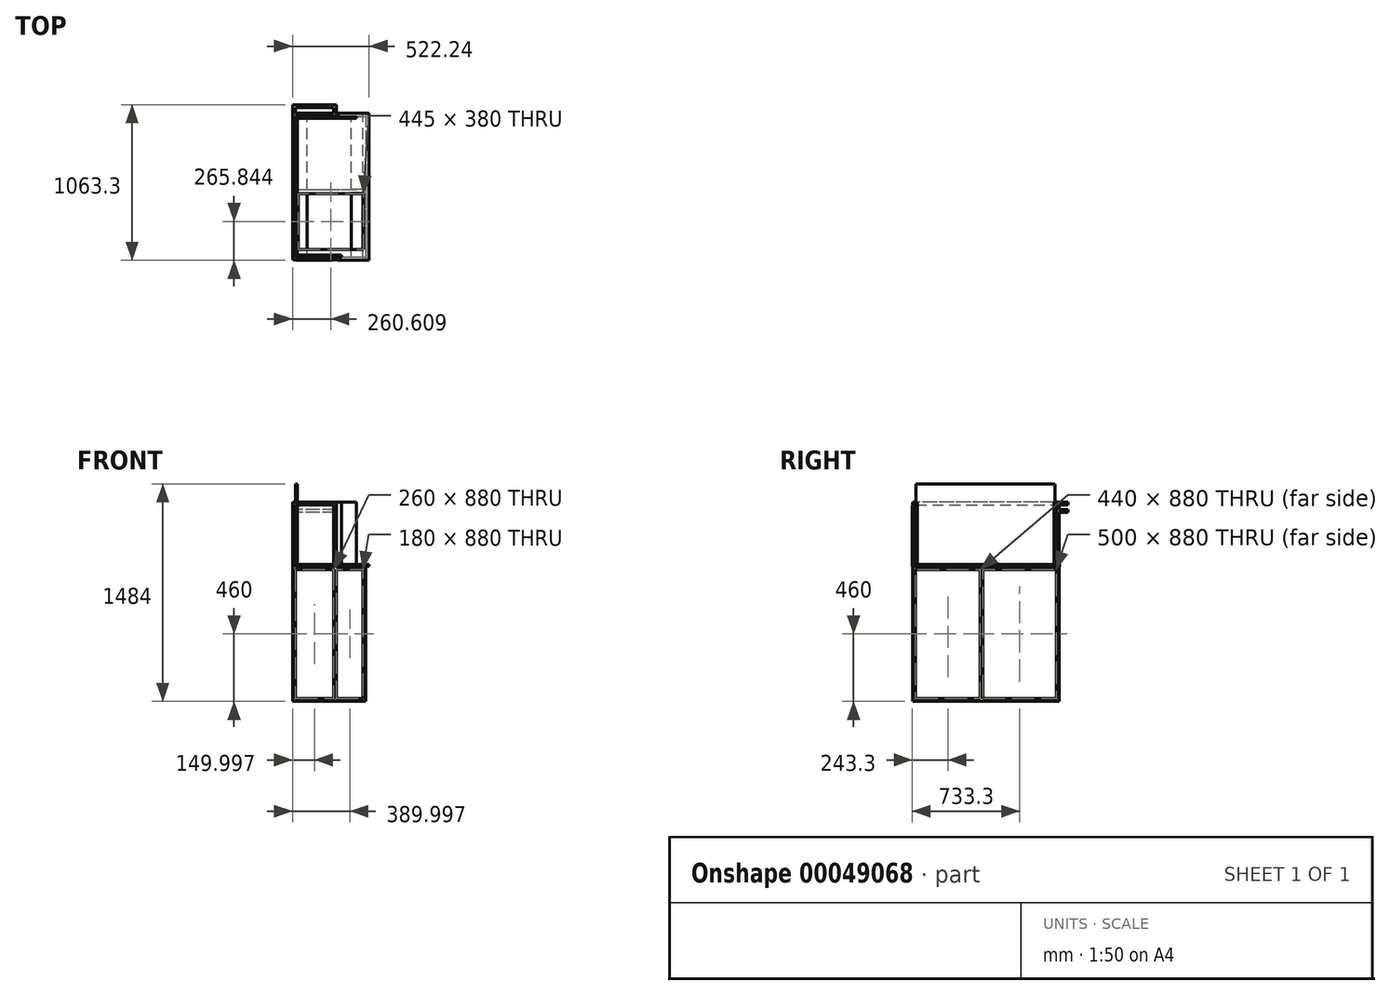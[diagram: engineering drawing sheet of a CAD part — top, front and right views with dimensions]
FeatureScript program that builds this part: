
annotation { "Feature Type Name" : "Feature", "Feature Type Description" : "" }
export const myFeature = defineFeature(function(context is Context, id is Id, definition is map)
    precondition{}
    {
        {
            var Q0;
            Q0=qCreatedBy(makeId("Top.planeOp"),FACE);
            var sketch = newSketch(context, id + "F0", { "sketchPlane" : qUnion([Q0])});
            skLineSegment(sketch, "E0.bottom", {"start": v(-100.51, 520.1) * mm, "end": v(399.49, 520.1) * mm});
            skLineSegment(sketch, "E0.top", {"start": v(-100.51, -479.9) * mm, "end": v(399.49, -479.9) * mm});
            skLineSegment(sketch, "E0.left", {"start": v(-100.51, 520.1) * mm, "end": v(-100.51, -479.9) * mm});
            skLineSegment(sketch, "E0.right", {"start": v(399.49, 520.1) * mm, "end": v(399.49, -479.9) * mm});
            skLineSegment(sketch, "E1.bottom", {"start": v(-80.51, 500.1) * mm, "end": v(379.49, 500.1) * mm});
            skLineSegment(sketch, "E1.top", {"start": v(-80.51, -459.9) * mm, "end": v(379.49, -459.9) * mm});
            skLineSegment(sketch, "E1.left", {"start": v(-80.51, 500.1) * mm, "end": v(-80.51, -459.9) * mm});
            skLineSegment(sketch, "E1.right", {"start": v(379.49, 500.1) * mm, "end": v(379.49, -459.9) * mm});
            skSolve(sketch);
        }
        {
            var Q0;
            Q0=makeQuery(id+"F0.imprint","IMPRINT",FACE,{"disambiguationData":[TD([[makeQuery(id+"F0.imprint","IMPRINT",EDGE,{"derivedFrom":sQuery(id+"F0.wireOp",EDGE,"E0.bottom")}),-1.0]])]});
            extrude(context, id + "F1", {"entities" : qUnion([Q0]), "depth" : 20 * mm});
        }
        {
            var Q0;
            Q0=makeQuery(id+"F1.opExtrude","CAP_FACE",FACE,{"disambiguationData":[OSD([sQuery(id+"F0.wireOp",EDGE,"E0.bottom"),sQuery(id+"F0.wireOp",EDGE,"E0.top"),sQuery(id+"F0.wireOp",EDGE,"E0.left"),sQuery(id+"F0.wireOp",EDGE,"E0.right"),sQuery(id+"F0.wireOp",EDGE,"E1.bottom"),sQuery(id+"F0.wireOp",EDGE,"E1.top"),sQuery(id+"F0.wireOp",EDGE,"E1.left"),sQuery(id+"F0.wireOp",EDGE,"E1.right")])],"isStart":false});
            var sketch = newSketch(context, id + "F2", { "sketchPlane" : qUnion([Q0])});
            skLineSegment(sketch, "E2.bottom", {"start": v(-100.51, 520.1) * mm, "end": v(-80.51, 520.1) * mm});
            skLineSegment(sketch, "E2.top", {"start": v(-100.51, 500.1) * mm, "end": v(-80.51, 500.1) * mm});
            skLineSegment(sketch, "E2.left", {"start": v(-100.51, 520.1) * mm, "end": v(-100.51, 500.1) * mm});
            skLineSegment(sketch, "E2.right", {"start": v(-80.51, 520.1) * mm, "end": v(-80.51, 500.1) * mm});
            skLineSegment(sketch, "E3.bottom", {"start": v(-100.51, -479.9) * mm, "end": v(-80.51, -479.9) * mm});
            skLineSegment(sketch, "E3.top", {"start": v(-100.51, -459.9) * mm, "end": v(-80.51, -459.9) * mm});
            skLineSegment(sketch, "E3.left", {"start": v(-100.51, -479.9) * mm, "end": v(-100.51, -459.9) * mm});
            skLineSegment(sketch, "E3.right", {"start": v(-80.51, -479.9) * mm, "end": v(-80.51, -459.9) * mm});
            skLineSegment(sketch, "E4.bottom", {"start": v(179.49, -459.9) * mm, "end": v(199.49, -459.9) * mm});
            skLineSegment(sketch, "E4.top", {"start": v(179.49, -479.9) * mm, "end": v(199.49, -479.9) * mm});
            skLineSegment(sketch, "E4.left", {"start": v(199.49, -459.9) * mm, "end": v(199.49, -479.9) * mm});
            skLineSegment(sketch, "E4.right", {"start": v(179.49, -459.9) * mm, "end": v(179.49, -479.9) * mm});
            skLineSegment(sketch, "E5.bottom", {"start": v(179.49, 520.1) * mm, "end": v(199.49, 520.1) * mm});
            skLineSegment(sketch, "E5.top", {"start": v(179.49, 500.1) * mm, "end": v(199.49, 500.1) * mm});
            skLineSegment(sketch, "E5.left", {"start": v(179.49, 520.1) * mm, "end": v(179.49, 500.1) * mm});
            skLineSegment(sketch, "E5.right", {"start": v(199.49, 520.1) * mm, "end": v(199.49, 500.1) * mm});
            skSolve(sketch);
        }
        {
            var Q0;
            Q0 = qSketchRegion(id + "F2", true);
            extrude(context, id + "F3", {"entities" : qUnion([Q0]), "operationType" : NewBodyOperationType.ADD, "depth" : 1340 * mm});
        }
        {
            var Q0;
            {var subQ0=sQuery(id+"F0.wireOp",EDGE,"E0.bottom");var subQ1=sQuery(id+"F0.wireOp",EDGE,"E0.top");var subQ2=sQuery(id+"F0.wireOp",EDGE,"E0.right");var subQ3=sQuery(id+"F0.wireOp",EDGE,"E1.bottom");var subQ4=sQuery(id+"F0.wireOp",EDGE,"E1.top");var subQ5=sQuery(id+"F0.wireOp",EDGE,"E1.right");Q0=makeQuery(id+"F3.boolean.opBoolean","SPLIT",FACE,{"disambiguationData":[TD([makeQuery(id+"F1.opExtrude","SWEPT_FACE",FACE,{"disambiguationData":[OSD([subQ2])]})])],"derivedFrom":makeQuery(id+"F1.opExtrude","CAP_FACE",FACE,{"disambiguationData":[OSD([subQ0,subQ1,sQuery(id+"F0.wireOp",EDGE,"E0.left"),subQ2,subQ3,subQ4,sQuery(id+"F0.wireOp",EDGE,"E1.left"),subQ5])],"isStart":false})});}
            var sketch = newSketch(context, id + "F4", { "sketchPlane" : qUnion([Q0])});
            skLineSegment(sketch, "E6.bottom", {"start": v(379.49, 500.1) * mm, "end": v(399.49, 500.1) * mm});
            skLineSegment(sketch, "E6.top", {"start": v(379.49, 520.1) * mm, "end": v(399.49, 520.1) * mm});
            skLineSegment(sketch, "E6.left", {"start": v(379.49, 500.1) * mm, "end": v(379.49, 520.1) * mm});
            skLineSegment(sketch, "E6.right", {"start": v(399.49, 500.1) * mm, "end": v(399.49, 520.1) * mm});
            skLineSegment(sketch, "E7.bottom", {"start": v(379.49, -459.9) * mm, "end": v(399.49, -459.9) * mm});
            skLineSegment(sketch, "E7.top", {"start": v(379.49, -479.9) * mm, "end": v(399.49, -479.9) * mm});
            skLineSegment(sketch, "E7.left", {"start": v(379.49, -459.9) * mm, "end": v(379.49, -479.9) * mm});
            skLineSegment(sketch, "E7.right", {"start": v(399.49, -459.9) * mm, "end": v(399.49, -479.9) * mm});
            skSolve(sketch);
        }
        {
            var Q0;
            Q0 = qSketchRegion(id + "F4", true);
            extrude(context, id + "F5", {"entities" : qUnion([Q0]), "operationType" : NewBodyOperationType.ADD, "depth" : 900 * mm});
        }
        {
            var Q0;
            Q0=makeQuery(id+"F5.opExtrude","SWEPT_FACE",FACE,{"disambiguationData":[OSD([sQuery(id+"F4.wireOp",EDGE,"E6.bottom")])]});
            var sketch = newSketch(context, id + "F6", { "sketchPlane" : qUnion([Q0])});
            skLineSegment(sketch, "E8.bottom", {"start": v(379.49, 920) * mm, "end": v(399.49, 920) * mm});
            skLineSegment(sketch, "E8.top", {"start": v(379.49, 900) * mm, "end": v(399.49, 900) * mm});
            skLineSegment(sketch, "E8.left", {"start": v(379.49, 920) * mm, "end": v(379.49, 900) * mm});
            skLineSegment(sketch, "E8.right", {"start": v(399.49, 920) * mm, "end": v(399.49, 900) * mm});
            skSolve(sketch);
        }
        {
            var Q0;
            Q0 = qSketchRegion(id + "F6", true);
            extrude(context, id + "F7", {"entities" : qUnion([Q0]), "operationType" : NewBodyOperationType.ADD, "endBound" : BoundingType.UP_TO_NEXT, "depth" : 25 * mm});
        }
        {
            var Q0;
            Q0=makeQuery(id+"F7.boolean.opBoolean","MERGE",FACE,{"derivedFrom":[makeQuery(id+"F5.opExtrude","SWEPT_FACE",FACE,{"disambiguationData":[OSD([sQuery(id+"F4.wireOp",EDGE,"E6.left")])]}),makeQuery(id+"F5.opExtrude","SWEPT_FACE",FACE,{"disambiguationData":[OSD([sQuery(id+"F4.wireOp",EDGE,"E7.left")])]}),makeQuery(id+"F7.opExtrude","SWEPT_FACE",FACE,{"disambiguationData":[OSD([sQuery(id+"F6.wireOp",EDGE,"E8.left")])]})]});
            var sketch = newSketch(context, id + "F8", { "sketchPlane" : qUnion([Q0])});
            skLineSegment(sketch, "E9.bottom", {"start": v(459.9, 900) * mm, "end": v(479.9, 900) * mm});
            skLineSegment(sketch, "E9.top", {"start": v(459.9, 920) * mm, "end": v(479.9, 920) * mm});
            skLineSegment(sketch, "E9.left", {"start": v(459.9, 900) * mm, "end": v(459.9, 920) * mm});
            skLineSegment(sketch, "E9.right", {"start": v(479.9, 900) * mm, "end": v(479.9, 920) * mm});
            skLineSegment(sketch, "E10.bottom", {"start": v(-520.1, 920) * mm, "end": v(-500.1, 920) * mm});
            skLineSegment(sketch, "E10.top", {"start": v(-520.1, 900) * mm, "end": v(-500.1, 900) * mm});
            skLineSegment(sketch, "E10.left", {"start": v(-520.1, 920) * mm, "end": v(-520.1, 900) * mm});
            skLineSegment(sketch, "E10.right", {"start": v(-500.1, 920) * mm, "end": v(-500.1, 900) * mm});
            skSolve(sketch);
        }
        {
            var Q0;
            Q0 = qSketchRegion(id + "F8", true);
            extrude(context, id + "F9", {"entities" : qUnion([Q0]), "operationType" : NewBodyOperationType.ADD, "endBound" : BoundingType.UP_TO_NEXT, "depth" : 25 * mm});
        }
        {
            var Q0;
            {var subQ0=sQuery(id+"F0.wireOp",EDGE,"E0.bottom");var subQ1=sQuery(id+"F0.wireOp",EDGE,"E0.top");var subQ2=sQuery(id+"F0.wireOp",EDGE,"E0.right");var subQ3=sQuery(id+"F0.wireOp",EDGE,"E1.bottom");var subQ4=sQuery(id+"F0.wireOp",EDGE,"E1.top");var subQ5=sQuery(id+"F0.wireOp",EDGE,"E1.right");var subQ6=makeQuery(id+"F1.opExtrude","CAP_FACE",FACE,{"disambiguationData":[OSD([subQ0,subQ1,sQuery(id+"F0.wireOp",EDGE,"E0.left"),subQ2,subQ3,subQ4,sQuery(id+"F0.wireOp",EDGE,"E1.left"),subQ5])],"isStart":false});var subQ8=makeQuery(id+"F1.opExtrude","SWEPT_FACE",FACE,{"disambiguationData":[OSD([subQ2])]});Q0=makeQuery(id+"F5.boolean.opBoolean","SPLIT",FACE,{"disambiguationData":[TD([subQ8])],"derivedFrom":makeQuery(id+"F3.boolean.opBoolean","SPLIT",FACE,{"disambiguationData":[TD([subQ8])],"derivedFrom":subQ6})});}
            var sketch = newSketch(context, id + "F10", { "sketchPlane" : qUnion([Q0])});
            skLineSegment(sketch, "E11.bottom", {"start": v(379.49, 0.1) * mm, "end": v(399.49, 0.1) * mm});
            skLineSegment(sketch, "E11.top", {"start": v(379.49, -19.9) * mm, "end": v(399.49, -19.9) * mm});
            skLineSegment(sketch, "E11.left", {"start": v(379.49, -19.9) * mm, "end": v(379.49, 0.1) * mm});
            skLineSegment(sketch, "E11.right", {"start": v(399.49, -19.9) * mm, "end": v(399.49, 0.1) * mm});
            skSolve(sketch);
        }
        {
            var Q0;
            Q0 = qSketchRegion(id + "F10", true);
            extrude(context, id + "F11", {"entities" : qUnion([Q0]), "operationType" : NewBodyOperationType.ADD, "endBound" : BoundingType.UP_TO_NEXT, "depth" : 25 * mm});
        }
        {
            var Q0;
            {var subQ0=sQuery(id+"F4.wireOp",EDGE,"E6.left");var subQ1=makeQuery(id+"F5.opExtrude","SWEPT_FACE",FACE,{"disambiguationData":[OSD([subQ0])]});var subQ2=sQuery(id+"F4.wireOp",EDGE,"E7.left");var subQ3=makeQuery(id+"F5.opExtrude","SWEPT_FACE",FACE,{"disambiguationData":[OSD([subQ2])]});var subQ4=makeQuery(id+"F7.opExtrude","SWEPT_FACE",FACE,{"disambiguationData":[OSD([sQuery(id+"F6.wireOp",EDGE,"E8.left")])]});Q0=makeQuery(id+"F11.boolean.opBoolean","MERGE",FACE,{"derivedFrom":[makeQuery(id+"F1.opExtrude","SWEPT_FACE",FACE,{"disambiguationData":[OSD([sQuery(id+"F0.wireOp",EDGE,"E1.right")])]}),makeQuery(id+"F9.boolean.opBoolean","SPLIT",FACE,{"disambiguationData":[TD([makeQuery(id+"F7.opExtrude","SWEPT_FACE",FACE,{"disambiguationData":[OSD([sQuery(id+"F6.wireOp",EDGE,"E8.bottom")])]})])],"derivedFrom":makeQuery(id+"F7.boolean.opBoolean","MERGE",FACE,{"derivedFrom":[subQ1,subQ3,subQ4]})}),makeQuery(id+"F11.opExtrude","SWEPT_FACE",FACE,{"disambiguationData":[OSD([sQuery(id+"F10.wireOp",EDGE,"E11.left")])]})]});}
            var sketch = newSketch(context, id + "F12", { "sketchPlane" : qUnion([Q0])});
            skLineSegment(sketch, "E12.bottom", {"start": v(-0.1, 20) * mm, "end": v(19.9, 20) * mm});
            skLineSegment(sketch, "E12.top", {"start": v(-0.1, 0) * mm, "end": v(19.9, 0) * mm});
            skLineSegment(sketch, "E12.left", {"start": v(-0.1, 20) * mm, "end": v(-0.1, 0) * mm});
            skLineSegment(sketch, "E12.right", {"start": v(19.9, 20) * mm, "end": v(19.9, 0) * mm});
            skSolve(sketch);
        }
        {
            var Q0;
            Q0 = qSketchRegion(id + "F12", true);
            extrude(context, id + "F13", {"entities" : qUnion([Q0]), "operationType" : NewBodyOperationType.ADD, "endBound" : BoundingType.UP_TO_NEXT, "depth" : 25 * mm});
        }
        {
            var Q0;
            {var subQ0=makeQuery(id+"F3.opExtrude","SWEPT_FACE",FACE,{"disambiguationData":[OSD([sQuery(id+"F2.wireOp",EDGE,"E2.top")])]});var subQ1=sQuery(id+"F0.wireOp",EDGE,"E1.bottom");var subQ2=makeQuery(id+"F1.opExtrude","SWEPT_FACE",FACE,{"disambiguationData":[OSD([subQ1])]});var subQ3=makeQuery(id+"F3.opExtrude","SWEPT_FACE",FACE,{"disambiguationData":[OSD([sQuery(id+"F2.wireOp",EDGE,"E5.top")])]});var subQ4=makeQuery(id+"FL1WmcuwInFp1yL_1.opExtrude","SWEPT_FACE",FACE,{"disambiguationData":[OSD([sQuery(id+"FAQpi5QERm3sSWY_1.wireOp",EDGE,"ee50a77b-da70-4ba3-90c0-c1dc34b9897d.left")])]});var subQ6=sQuery(id+"F0.wireOp",EDGE,"E0.left");Q0=makeQuery(id+"FbzhfKtn9ych7IT_1.boolean.opBoolean","SPLIT",FACE,{"disambiguationData":[TD([makeQuery(id+"F1.opExtrude","SWEPT_FACE",FACE,{"disambiguationData":[OSD([subQ6])]})])],"derivedFrom":makeQuery(id+"FL1WmcuwInFp1yL_1.boolean.opBoolean","MERGE",FACE,{"derivedFrom":[subQ0,makeQuery(id+"F3.boolean.opBoolean","MERGE",FACE,{"derivedFrom":[subQ2,subQ3]}),subQ4]})});}
            var sketch = newSketch(context, id + "F14", { "sketchPlane" : qUnion([Q0])});
            skLineSegment(sketch, "E13.bottom", {"start": v(-100.51, 920) * mm, "end": v(-80.51, 920) * mm});
            skLineSegment(sketch, "E13.top", {"start": v(-100.51, 900) * mm, "end": v(-80.51, 900) * mm});
            skLineSegment(sketch, "E13.left", {"start": v(-100.51, 920) * mm, "end": v(-100.51, 900) * mm});
            skLineSegment(sketch, "E13.right", {"start": v(-80.51, 920) * mm, "end": v(-80.51, 900) * mm});
            skSolve(sketch);
        }
        {
            var Q0;
            Q0 = qSketchRegion(id + "F14", true);
            extrude(context, id + "F15", {"entities" : qUnion([Q0]), "operationType" : NewBodyOperationType.ADD, "endBound" : BoundingType.UP_TO_NEXT, "depth" : 25 * mm});
        }
        {
            var Q0;
            {var subQ0=makeQuery(id+"F3.opExtrude","SWEPT_FACE",FACE,{"disambiguationData":[OSD([sQuery(id+"F2.wireOp",EDGE,"E3.right")])]});var subQ1=makeQuery(id+"FbzhfKtn9ych7IT_1.opExtrude","SWEPT_FACE",FACE,{"disambiguationData":[OSD([sQuery(id+"FmSU7zEhJE57HWf_1.wireOp",EDGE,"9a584f31-96d2-4139-bbb7-4ec877bc2097.right")])]});var subQ3=sQuery(id+"F0.wireOp",EDGE,"E0.top");Q0=makeQuery(id+"F15.boolean.opBoolean","MERGE",FACE,{"derivedFrom":[makeQuery(id+"F3.opExtrude","SWEPT_FACE",FACE,{"disambiguationData":[OSD([sQuery(id+"F2.wireOp",EDGE,"E2.right")])]}),makeQuery(id+"FyYalR2EVa5J6ih_1.boolean.opBoolean","SPLIT",FACE,{"disambiguationData":[TD([makeQuery(id+"F1.opExtrude","SWEPT_FACE",FACE,{"disambiguationData":[OSD([subQ3])]})])],"derivedFrom":makeQuery(id+"FbzhfKtn9ych7IT_1.boolean.opBoolean","MERGE",FACE,{"derivedFrom":[subQ0,subQ1]})}),makeQuery(id+"F15.opExtrude","SWEPT_FACE",FACE,{"disambiguationData":[OSD([sQuery(id+"F14.wireOp",EDGE,"E13.right")])]})]});}
            var sketch = newSketch(context, id + "F16", { "sketchPlane" : qUnion([Q0])});
            skLineSegment(sketch, "E14.bottom", {"start": v(-459.9, 920) * mm, "end": v(-479.9, 920) * mm});
            skLineSegment(sketch, "E14.top", {"start": v(-459.9, 900) * mm, "end": v(-479.9, 900) * mm});
            skLineSegment(sketch, "E14.left", {"start": v(-459.9, 920) * mm, "end": v(-459.9, 900) * mm});
            skLineSegment(sketch, "E14.right", {"start": v(-479.9, 920) * mm, "end": v(-479.9, 900) * mm});
            skLineSegment(sketch, "E15.bottom", {"start": v(500.1, 920) * mm, "end": v(520.1, 920) * mm});
            skLineSegment(sketch, "E15.top", {"start": v(500.1, 900) * mm, "end": v(520.1, 900) * mm});
            skLineSegment(sketch, "E15.left", {"start": v(500.1, 920) * mm, "end": v(500.1, 900) * mm});
            skLineSegment(sketch, "E15.right", {"start": v(520.1, 920) * mm, "end": v(520.1, 900) * mm});
            skSolve(sketch);
        }
        {
            var Q0;
            Q0 = qSketchRegion(id + "F16", true);
            extrude(context, id + "F17", {"entities" : qUnion([Q0]), "operationType" : NewBodyOperationType.ADD, "endBound" : BoundingType.UP_TO_NEXT, "depth" : 25 * mm});
        }
        {
            var Q0;
            {var subQ0=sQuery(id+"F0.wireOp",EDGE,"E0.left");var subQ1=sQuery(id+"F0.wireOp",EDGE,"E1.bottom");var subQ2=sQuery(id+"F0.wireOp",EDGE,"E1.top");var subQ3=sQuery(id+"F0.wireOp",EDGE,"E1.left");var subQ4=makeQuery(id+"F1.opExtrude","CAP_FACE",FACE,{"disambiguationData":[OSD([sQuery(id+"F0.wireOp",EDGE,"E0.bottom"),sQuery(id+"F0.wireOp",EDGE,"E0.top"),subQ0,sQuery(id+"F0.wireOp",EDGE,"E0.right"),subQ1,subQ2,subQ3,sQuery(id+"F0.wireOp",EDGE,"E1.right")])],"isStart":false});Q0=makeQuery(id+"F13.boolean.opBoolean","MERGE",FACE,{"derivedFrom":[makeQuery(id+"F3.boolean.opBoolean","SPLIT",FACE,{"disambiguationData":[TD([makeQuery(id+"F1.opExtrude","SWEPT_FACE",FACE,{"disambiguationData":[OSD([subQ0])]})])],"derivedFrom":subQ4}),makeQuery(id+"F13.opExtrude","SWEPT_FACE",FACE,{"disambiguationData":[OSD([sQuery(id+"F12.wireOp",EDGE,"E12.bottom")])]})]});}
            var sketch = newSketch(context, id + "F18", { "sketchPlane" : qUnion([Q0])});
            skLineSegment(sketch, "E16.bottom", {"start": v(-80.51, 0.1) * mm, "end": v(-100.51, 0.1) * mm});
            skLineSegment(sketch, "E16.top", {"start": v(-80.51, -19.9) * mm, "end": v(-100.51, -19.9) * mm});
            skLineSegment(sketch, "E16.left", {"start": v(-80.51, 0.1) * mm, "end": v(-80.51, -19.9) * mm});
            skLineSegment(sketch, "E16.right", {"start": v(-100.51, 0.1) * mm, "end": v(-100.51, -19.9) * mm});
            skSolve(sketch);
        }
        {
            var Q0;
            Q0 = qSketchRegion(id + "F18", true);
            extrude(context, id + "F19", {"entities" : qUnion([Q0]), "operationType" : NewBodyOperationType.ADD, "endBound" : BoundingType.UP_TO_NEXT, "depth" : 25 * mm});
        }
        {
            var Q0;
            {var subQ0=sQuery(id+"F0.wireOp",EDGE,"E1.right");var subQ1=makeQuery(id+"F1.opExtrude","SWEPT_FACE",FACE,{"disambiguationData":[OSD([subQ0])]});var subQ2=sQuery(id+"F4.wireOp",EDGE,"E6.left");var subQ3=makeQuery(id+"F5.opExtrude","SWEPT_FACE",FACE,{"disambiguationData":[OSD([subQ2])]});var subQ4=sQuery(id+"F4.wireOp",EDGE,"E7.left");var subQ5=makeQuery(id+"F5.opExtrude","SWEPT_FACE",FACE,{"disambiguationData":[OSD([subQ4])]});var subQ6=makeQuery(id+"F7.opExtrude","SWEPT_FACE",FACE,{"disambiguationData":[OSD([sQuery(id+"F6.wireOp",EDGE,"E8.left")])]});var subQ7=makeQuery(id+"F9.opExtrude","SWEPT_FACE",FACE,{"disambiguationData":[OSD([sQuery(id+"F8.wireOp",EDGE,"E10.bottom")])]});var subQ8=makeQuery(id+"F9.opExtrude","SWEPT_FACE",FACE,{"disambiguationData":[OSD([sQuery(id+"F8.wireOp",EDGE,"E9.left")])]});var subQ9=makeQuery(id+"F9.opExtrude","SWEPT_FACE",FACE,{"disambiguationData":[OSD([sQuery(id+"F8.wireOp",EDGE,"E9.top")])]});var subQ10=makeQuery(id+"F9.opExtrude","SWEPT_FACE",FACE,{"disambiguationData":[OSD([sQuery(id+"F8.wireOp",EDGE,"E10.top")])]});var subQ11=makeQuery(id+"F9.opExtrude","SWEPT_FACE",FACE,{"disambiguationData":[OSD([sQuery(id+"F8.wireOp",EDGE,"E9.bottom")])]});var subQ12=makeQuery(id+"F7.opExtrude","SWEPT_FACE",FACE,{"disambiguationData":[OSD([sQuery(id+"F6.wireOp",EDGE,"E8.bottom")])]});var subQ13=makeQuery(id+"F7.opExtrude","SWEPT_FACE",FACE,{"disambiguationData":[OSD([sQuery(id+"F6.wireOp",EDGE,"E8.top")])]});var subQ14=makeQuery(id+"F3.opExtrude","SWEPT_FACE",FACE,{"disambiguationData":[OSD([sQuery(id+"F2.wireOp",EDGE,"E2.top")])]});var subQ15=sQuery(id+"F0.wireOp",EDGE,"E1.top");var subQ16=makeQuery(id+"F1.opExtrude","SWEPT_FACE",FACE,{"disambiguationData":[OSD([subQ15])]});var subQ17=sQuery(id+"F0.wireOp",EDGE,"E1.bottom");var subQ18=makeQuery(id+"F1.opExtrude","SWEPT_FACE",FACE,{"disambiguationData":[OSD([subQ17])]});var subQ19=makeQuery(id+"F3.opExtrude","SWEPT_FACE",FACE,{"disambiguationData":[OSD([sQuery(id+"F2.wireOp",EDGE,"E4.bottom")])]});var subQ20=makeQuery(id+"F3.opExtrude","SWEPT_FACE",FACE,{"disambiguationData":[OSD([sQuery(id+"F2.wireOp",EDGE,"E5.top")])]});var subQ21=sQuery(id+"F4.wireOp",EDGE,"E7.bottom");var subQ22=makeQuery(id+"F5.opExtrude","CAP_FACE",FACE,{"disambiguationData":[OSD([subQ21,sQuery(id+"F4.wireOp",EDGE,"E7.top"),subQ4,sQuery(id+"F4.wireOp",EDGE,"E7.right")])],"isStart":false});var subQ23=makeQuery(id+"FL1WmcuwInFp1yL_1.opExtrude","SWEPT_FACE",FACE,{"disambiguationData":[OSD([sQuery(id+"FAQpi5QERm3sSWY_1.wireOp",EDGE,"ee50a77b-da70-4ba3-90c0-c1dc34b9897d.left")])]});var subQ24=makeQuery(id+"F5.opExtrude","SWEPT_FACE",FACE,{"disambiguationData":[OSD([subQ21])]});var subQ25=sQuery(id+"F4.wireOp",EDGE,"E6.bottom");var subQ26=makeQuery(id+"F5.opExtrude","SWEPT_FACE",FACE,{"disambiguationData":[OSD([subQ25])]});var subQ27=makeQuery(id+"F9.opExtrude","SWEPT_FACE",FACE,{"disambiguationData":[OSD([sQuery(id+"F8.wireOp",EDGE,"E10.right")])]});var subQ28=makeQuery(id+"F5.opExtrude","CAP_FACE",FACE,{"disambiguationData":[OSD([subQ25,sQuery(id+"F4.wireOp",EDGE,"E6.top"),subQ2,sQuery(id+"F4.wireOp",EDGE,"E6.right")])],"isStart":false});var subQ29=makeQuery(id+"F11.opExtrude","SWEPT_FACE",FACE,{"disambiguationData":[OSD([sQuery(id+"F10.wireOp",EDGE,"E11.left")])]});Q0=makeQuery(id+"F13.boolean.opBoolean","SPLIT",FACE,{"disambiguationData":[TD([makeQuery(id+"F1.opExtrude","CAP_FACE",FACE,{"disambiguationData":[OSD([sQuery(id+"F0.wireOp",EDGE,"E0.bottom"),sQuery(id+"F0.wireOp",EDGE,"E0.top"),sQuery(id+"F0.wireOp",EDGE,"E0.left"),sQuery(id+"F0.wireOp",EDGE,"E0.right"),subQ17,subQ15,sQuery(id+"F0.wireOp",EDGE,"E1.left"),subQ0])],"isStart":false}),subQ18,subQ16,subQ1,subQ14,subQ19,subQ20,subQ23,subQ26,subQ28,subQ3,subQ24,subQ22,subQ5,subQ12,subQ13,subQ6,subQ11,subQ9,subQ8,subQ7,subQ10,subQ27,makeQuery(id+"F11.opExtrude","SWEPT_FACE",FACE,{"disambiguationData":[OSD([sQuery(id+"F10.wireOp",EDGE,"E11.bottom")])]}),makeQuery(id+"F11.opExtrude","SWEPT_FACE",FACE,{"disambiguationData":[OSD([sQuery(id+"F10.wireOp",EDGE,"E11.top")])]}),subQ29,makeQuery(id+"F13.opExtrude","SWEPT_FACE",FACE,{"disambiguationData":[OSD([sQuery(id+"F12.wireOp",EDGE,"E12.bottom")])]}),makeQuery(id+"F13.opExtrude","SWEPT_FACE",FACE,{"disambiguationData":[OSD([sQuery(id+"F12.wireOp",EDGE,"E12.left")])]}),makeQuery(id+"F13.opExtrude","SWEPT_FACE",FACE,{"disambiguationData":[OSD([sQuery(id+"F12.wireOp",EDGE,"E12.right")])]})])],"derivedFrom":makeQuery(id+"F11.boolean.opBoolean","MERGE",FACE,{"derivedFrom":[subQ1,makeQuery(id+"F9.boolean.opBoolean","SPLIT",FACE,{"disambiguationData":[TD([subQ12])],"derivedFrom":makeQuery(id+"F7.boolean.opBoolean","MERGE",FACE,{"derivedFrom":[subQ3,subQ5,subQ6]})}),subQ29]})});}
            var sketch = newSketch(context, id + "F20", { "sketchPlane" : qUnion([Q0])});
            skLineSegment(sketch, "E17.bottom", {"start": v(-0.1, 900) * mm, "end": v(19.9, 900) * mm});
            skLineSegment(sketch, "E17.top", {"start": v(-0.1, 920) * mm, "end": v(19.9, 920) * mm});
            skLineSegment(sketch, "E17.left", {"start": v(-0.1, 900) * mm, "end": v(-0.1, 920) * mm});
            skLineSegment(sketch, "E17.right", {"start": v(19.9, 900) * mm, "end": v(19.9, 920) * mm});
            skSolve(sketch);
        }
        {
            var Q0;
            Q0 = qSketchRegion(id + "F20", true);
            extrude(context, id + "F21", {"entities" : qUnion([Q0]), "operationType" : NewBodyOperationType.ADD, "endBound" : BoundingType.UP_TO_NEXT, "depth" : 25 * mm});
        }
        {
            var Q0;
            {var subQ0=sQuery(id+"F2.wireOp",EDGE,"E2.top");Q0=makeQuery(id+"F15.boolean.opBoolean","SPLIT",FACE,{"disambiguationData":[TD([makeQuery(id+"F15.opExtrude","SWEPT_FACE",FACE,{"disambiguationData":[OSD([sQuery(id+"F14.wireOp",EDGE,"E13.bottom")])]})])],"derivedFrom":makeQuery(id+"F3.opExtrude","SWEPT_FACE",FACE,{"disambiguationData":[OSD([subQ0])]})});}
            var sketch = newSketch(context, id + "F22", { "sketchPlane" : qUnion([Q0])});
            skLineSegment(sketch, "E18.bottom", {"start": v(-100.51, 1360) * mm, "end": v(-80.51, 1360) * mm});
            skLineSegment(sketch, "E18.top", {"start": v(-100.51, 1340) * mm, "end": v(-80.51, 1340) * mm});
            skLineSegment(sketch, "E18.left", {"start": v(-100.51, 1360) * mm, "end": v(-100.51, 1340) * mm});
            skLineSegment(sketch, "E18.right", {"start": v(-80.51, 1360) * mm, "end": v(-80.51, 1340) * mm});
            skSolve(sketch);
        }
        {
            var Q0;
            Q0 = qSketchRegion(id + "F22", true);
            extrude(context, id + "F23", {"entities" : qUnion([Q0]), "operationType" : NewBodyOperationType.ADD, "endBound" : BoundingType.UP_TO_NEXT, "depth" : 25 * mm});
        }
        {
            var Q0;
            {var subQ0=sQuery(id+"F2.wireOp",EDGE,"E2.right");var subQ1=makeQuery(id+"F3.opExtrude","SWEPT_FACE",FACE,{"disambiguationData":[OSD([subQ0])]});var subQ2=sQuery(id+"F2.wireOp",EDGE,"E3.right");var subQ3=makeQuery(id+"F3.opExtrude","SWEPT_FACE",FACE,{"disambiguationData":[OSD([subQ2])]});var subQ4=makeQuery(id+"F15.opExtrude","SWEPT_FACE",FACE,{"disambiguationData":[OSD([sQuery(id+"F14.wireOp",EDGE,"E13.right")])]});var subQ5=makeQuery(id+"F15.boolean.opBoolean","MERGE",FACE,{"derivedFrom":[subQ1,subQ3,subQ4]});var subQ6=sQuery(id+"F2.wireOp",EDGE,"E2.bottom");var subQ7=sQuery(id+"F2.wireOp",EDGE,"E2.top");var subQ8=makeQuery(id+"F15.opExtrude","SWEPT_FACE",FACE,{"disambiguationData":[OSD([sQuery(id+"F14.wireOp",EDGE,"E13.bottom")])]});var subQ9=sQuery(id+"F2.wireOp",EDGE,"E3.bottom");var subQ10=sQuery(id+"F2.wireOp",EDGE,"E3.top");Q0=makeQuery(id+"F23.boolean.opBoolean","MERGE",FACE,{"derivedFrom":[makeQuery(id+"F17.boolean.opBoolean","SPLIT",FACE,{"disambiguationData":[TD([makeQuery(id+"F1.opExtrude","SWEPT_FACE",FACE,{"disambiguationData":[OSD([sQuery(id+"F0.wireOp",EDGE,"E0.bottom")])]}),makeQuery(id+"F1.opExtrude","SWEPT_FACE",FACE,{"disambiguationData":[OSD([sQuery(id+"F0.wireOp",EDGE,"E1.bottom")])]}),makeQuery(id+"F3.opExtrude","SWEPT_FACE",FACE,{"disambiguationData":[OSD([subQ6])]}),makeQuery(id+"F3.opExtrude","CAP_FACE",FACE,{"disambiguationData":[OSD([subQ6,subQ7,sQuery(id+"F2.wireOp",EDGE,"E2.left"),subQ0])],"isStart":false}),makeQuery(id+"F3.opExtrude","SWEPT_FACE",FACE,{"disambiguationData":[OSD([subQ7])]}),subQ1,subQ3,makeQuery(id+"F3.opExtrude","SWEPT_FACE",FACE,{"disambiguationData":[OSD([sQuery(id+"F2.wireOp",EDGE,"E5.bottom")])]}),makeQuery(id+"F3.opExtrude","SWEPT_FACE",FACE,{"disambiguationData":[OSD([sQuery(id+"F2.wireOp",EDGE,"E5.top")])]}),makeQuery(id+"F5.opExtrude","SWEPT_FACE",FACE,{"disambiguationData":[OSD([sQuery(id+"F4.wireOp",EDGE,"E6.top")])]}),makeQuery(id+"F9.opExtrude","SWEPT_FACE",FACE,{"disambiguationData":[OSD([sQuery(id+"F8.wireOp",EDGE,"E10.left")])]}),makeQuery(id+"F9.opExtrude","SWEPT_FACE",FACE,{"disambiguationData":[OSD([sQuery(id+"F8.wireOp",EDGE,"E10.right")])]}),subQ8,subQ4,makeQuery(id+"F17.opExtrude","SWEPT_FACE",FACE,{"disambiguationData":[OSD([sQuery(id+"F16.wireOp",EDGE,"E15.bottom")])]}),makeQuery(id+"F17.opExtrude","SWEPT_FACE",FACE,{"disambiguationData":[OSD([sQuery(id+"F16.wireOp",EDGE,"E15.left")])]}),makeQuery(id+"F17.opExtrude","SWEPT_FACE",FACE,{"disambiguationData":[OSD([sQuery(id+"F16.wireOp",EDGE,"E15.right")])]})])],"derivedFrom":subQ5}),makeQuery(id+"F17.boolean.opBoolean","SPLIT",FACE,{"disambiguationData":[TD([makeQuery(id+"F1.opExtrude","SWEPT_FACE",FACE,{"disambiguationData":[OSD([sQuery(id+"F0.wireOp",EDGE,"E0.top")])]}),makeQuery(id+"F1.opExtrude","SWEPT_FACE",FACE,{"disambiguationData":[OSD([sQuery(id+"F0.wireOp",EDGE,"E1.top")])]}),subQ1,makeQuery(id+"F3.opExtrude","SWEPT_FACE",FACE,{"disambiguationData":[OSD([subQ9])]}),makeQuery(id+"F3.opExtrude","CAP_FACE",FACE,{"disambiguationData":[OSD([subQ9,subQ10,sQuery(id+"F2.wireOp",EDGE,"E3.left"),subQ2])],"isStart":false}),makeQuery(id+"F3.opExtrude","SWEPT_FACE",FACE,{"disambiguationData":[OSD([subQ10])]}),subQ3,makeQuery(id+"F3.opExtrude","SWEPT_FACE",FACE,{"disambiguationData":[OSD([sQuery(id+"F2.wireOp",EDGE,"E4.bottom")])]}),makeQuery(id+"F3.opExtrude","SWEPT_FACE",FACE,{"disambiguationData":[OSD([sQuery(id+"F2.wireOp",EDGE,"E4.top")])]}),makeQuery(id+"F5.opExtrude","SWEPT_FACE",FACE,{"disambiguationData":[OSD([sQuery(id+"F4.wireOp",EDGE,"E7.top")])]}),makeQuery(id+"F9.opExtrude","SWEPT_FACE",FACE,{"disambiguationData":[OSD([sQuery(id+"F8.wireOp",EDGE,"E9.left")])]}),makeQuery(id+"F9.opExtrude","SWEPT_FACE",FACE,{"disambiguationData":[OSD([sQuery(id+"F8.wireOp",EDGE,"E9.right")])]}),subQ8,subQ4,makeQuery(id+"F17.opExtrude","SWEPT_FACE",FACE,{"disambiguationData":[OSD([sQuery(id+"F16.wireOp",EDGE,"E14.bottom")])]}),makeQuery(id+"F17.opExtrude","SWEPT_FACE",FACE,{"disambiguationData":[OSD([sQuery(id+"F16.wireOp",EDGE,"E14.left")])]}),makeQuery(id+"F17.opExtrude","SWEPT_FACE",FACE,{"disambiguationData":[OSD([sQuery(id+"F16.wireOp",EDGE,"E14.right")])]})])],"derivedFrom":subQ5}),makeQuery(id+"F23.opExtrude","SWEPT_FACE",FACE,{"disambiguationData":[OSD([sQuery(id+"F22.wireOp",EDGE,"E18.right")])]})]});}
            var sketch = newSketch(context, id + "F24", { "sketchPlane" : qUnion([Q0])});
            skLineSegment(sketch, "E19.bottom", {"start": v(-479.9, 1360) * mm, "end": v(-459.9, 1360) * mm});
            skLineSegment(sketch, "E19.top", {"start": v(-479.9, 1340) * mm, "end": v(-459.9, 1340) * mm});
            skLineSegment(sketch, "E19.left", {"start": v(-479.9, 1360) * mm, "end": v(-479.9, 1340) * mm});
            skLineSegment(sketch, "E19.right", {"start": v(-459.9, 1360) * mm, "end": v(-459.9, 1340) * mm});
            skLineSegment(sketch, "E20.bottom", {"start": v(500.1, 1340) * mm, "end": v(520.1, 1340) * mm});
            skLineSegment(sketch, "E20.top", {"start": v(500.1, 1360) * mm, "end": v(520.1, 1360) * mm});
            skLineSegment(sketch, "E20.left", {"start": v(500.1, 1340) * mm, "end": v(500.1, 1360) * mm});
            skLineSegment(sketch, "E20.right", {"start": v(520.1, 1340) * mm, "end": v(520.1, 1360) * mm});
            skSolve(sketch);
        }
        {
            var Q0;
            Q0 = qSketchRegion(id + "F24", true);
            extrude(context, id + "F25", {"entities" : qUnion([Q0]), "operationType" : NewBodyOperationType.ADD, "endBound" : BoundingType.UP_TO_NEXT, "depth" : 25 * mm});
        }
        {
            var Q0;
            Q0=makeQuery(id+"F85Uv7rZhHDFAwa_1.boolean.opBoolean","MERGE",FACE,{"derivedFrom":[makeQuery(id+"FmlsiqtGIArLWjF_1.boolean.opBoolean","MERGE",FACE,{"derivedFrom":[makeQuery(id+"F25.boolean.opBoolean","MERGE",FACE,{"derivedFrom":[makeQuery(id+"F2x57JLdlEXWWYt_1.boolean.opBoolean","MERGE",FACE,{"derivedFrom":[makeQuery(id+"FlIw4lgxEwkVzeK_1.boolean.opBoolean","MERGE",FACE,{"derivedFrom":[makeQuery(id+"F17.boolean.opBoolean","MERGE",FACE,{"derivedFrom":[makeQuery(id+"F9.boolean.opBoolean","MERGE",FACE,{"derivedFrom":[makeQuery(id+"F5.boolean.opBoolean","MERGE",FACE,{"derivedFrom":[makeQuery(id+"F3.boolean.opBoolean","MERGE",FACE,{"derivedFrom":[makeQuery(id+"F1.opExtrude","SWEPT_FACE",FACE,{"disambiguationData":[OSD([sQuery(id+"F0.wireOp",EDGE,"E0.bottom")])]}),makeQuery(id+"F3.opExtrude","SWEPT_FACE",FACE,{"disambiguationData":[OSD([sQuery(id+"F2.wireOp",EDGE,"E2.bottom")])]}),makeQuery(id+"F3.opExtrude","SWEPT_FACE",FACE,{"disambiguationData":[OSD([sQuery(id+"F2.wireOp",EDGE,"E5.bottom")])]})]}),makeQuery(id+"F5.opExtrude","SWEPT_FACE",FACE,{"disambiguationData":[OSD([sQuery(id+"F4.wireOp",EDGE,"E6.top")])]})]}),makeQuery(id+"F9.opExtrude","SWEPT_FACE",FACE,{"disambiguationData":[OSD([sQuery(id+"F8.wireOp",EDGE,"E10.left")])]})]}),makeQuery(id+"F17.opExtrude","SWEPT_FACE",FACE,{"disambiguationData":[OSD([sQuery(id+"F16.wireOp",EDGE,"E15.right")])]})]}),makeQuery(id+"FlIw4lgxEwkVzeK_1.opExtrude","CAP_FACE",FACE,{"disambiguationData":[OSD([sQuery(id+"FkDYzAea1YsHphk_1.wireOp",EDGE,"9abe4d72-cff0-40be-8d55-3529e60cb41f.bottom"),sQuery(id+"FkDYzAea1YsHphk_1.wireOp",EDGE,"9abe4d72-cff0-40be-8d55-3529e60cb41f.top"),sQuery(id+"FkDYzAea1YsHphk_1.wireOp",EDGE,"9abe4d72-cff0-40be-8d55-3529e60cb41f.left"),sQuery(id+"FkDYzAea1YsHphk_1.wireOp",EDGE,"9abe4d72-cff0-40be-8d55-3529e60cb41f.right")])],"isStart":true})]}),makeQuery(id+"F2x57JLdlEXWWYt_1.opExtrude","CAP_FACE",FACE,{"disambiguationData":[OSD([sQuery(id+"FdXj0KOZ6fV0Bf7_1.wireOp",EDGE,"2ac3b409-db7b-46f2-a2e4-049f104b95cf.bottom"),sQuery(id+"FdXj0KOZ6fV0Bf7_1.wireOp",EDGE,"2ac3b409-db7b-46f2-a2e4-049f104b95cf.top"),sQuery(id+"FdXj0KOZ6fV0Bf7_1.wireOp",EDGE,"2ac3b409-db7b-46f2-a2e4-049f104b95cf.left"),sQuery(id+"FdXj0KOZ6fV0Bf7_1.wireOp",EDGE,"2ac3b409-db7b-46f2-a2e4-049f104b95cf.right")])],"isStart":true})]}),makeQuery(id+"F25.opExtrude","SWEPT_FACE",FACE,{"disambiguationData":[OSD([sQuery(id+"F24.wireOp",EDGE,"E20.right")])]})]}),makeQuery(id+"FmlsiqtGIArLWjF_1.opExtrude","SWEPT_FACE",FACE,{"disambiguationData":[OSD([sQuery(id+"F9PASD7YzdcTaxW_1.wireOp",EDGE,"aaf027d5-d421-491f-bd49-f5003cbc895b.top")])]}),makeQuery(id+"FmlsiqtGIArLWjF_1.opExtrude","SWEPT_FACE",FACE,{"disambiguationData":[OSD([sQuery(id+"F9PASD7YzdcTaxW_1.wireOp",EDGE,"8c24dee2-4859-4918-b62b-53ab4d53a5c6.top")])]})]}),makeQuery(id+"F85Uv7rZhHDFAwa_1.opExtrude","SWEPT_FACE",FACE,{"disambiguationData":[OSD([sQuery(id+"FFAFteAvz5Cuugt_1.wireOp",EDGE,"0af742db-d6e2-4e39-92e2-1c10abb64e47.right")])]})]});
            var sketch = newSketch(context, id + "F26", { "sketchPlane" : qUnion([Q0])});
            skLineSegment(sketch, "E21.bottom", {"start": v(-179.49, 1360) * mm, "end": v(-199.49, 1360) * mm});
            skLineSegment(sketch, "E21.top", {"start": v(-179.49, 1340) * mm, "end": v(-199.49, 1340) * mm});
            skLineSegment(sketch, "E21.left", {"start": v(-179.49, 1360) * mm, "end": v(-179.49, 1340) * mm});
            skLineSegment(sketch, "E21.right", {"start": v(-199.49, 1360) * mm, "end": v(-199.49, 1340) * mm});
            skLineSegment(sketch, "E22.bottom", {"start": v(80.51, 1340) * mm, "end": v(100.51, 1340) * mm});
            skLineSegment(sketch, "E22.top", {"start": v(80.51, 1360) * mm, "end": v(100.51, 1360) * mm});
            skLineSegment(sketch, "E22.left", {"start": v(80.51, 1340) * mm, "end": v(80.51, 1360) * mm});
            skLineSegment(sketch, "E22.right", {"start": v(100.51, 1340) * mm, "end": v(100.51, 1360) * mm});
            skLineSegment(sketch, "E23.bottom", {"start": v(-199.49, 1310) * mm, "end": v(-179.49, 1310) * mm});
            skLineSegment(sketch, "E23.top", {"start": v(-199.49, 1290) * mm, "end": v(-179.49, 1290) * mm});
            skLineSegment(sketch, "E23.left", {"start": v(-199.49, 1310) * mm, "end": v(-199.49, 1290) * mm});
            skLineSegment(sketch, "E23.right", {"start": v(-179.49, 1310) * mm, "end": v(-179.49, 1290) * mm});
            skLineSegment(sketch, "E24.bottom", {"start": v(80.51, 1310) * mm, "end": v(100.51, 1310) * mm});
            skLineSegment(sketch, "E24.top", {"start": v(80.51, 1290) * mm, "end": v(100.51, 1290) * mm});
            skLineSegment(sketch, "E24.left", {"start": v(80.51, 1310) * mm, "end": v(80.51, 1290) * mm});
            skLineSegment(sketch, "E24.right", {"start": v(100.51, 1310) * mm, "end": v(100.51, 1290) * mm});
            skSolve(sketch);
        }
        {
            var Q0;
            Q0 = qSketchRegion(id + "F26", true);
            extrude(context, id + "F27", {"entities" : qUnion([Q0]), "operationType" : NewBodyOperationType.ADD, "depth" : 60 * mm});
        }
        {
            var Q0;
            {var subQ0=sQuery(id+"F2.wireOp",EDGE,"E2.right");var subQ1=makeQuery(id+"F3.opExtrude","SWEPT_FACE",FACE,{"disambiguationData":[OSD([subQ0])]});var subQ2=sQuery(id+"F2.wireOp",EDGE,"E3.right");var subQ3=makeQuery(id+"F3.opExtrude","SWEPT_FACE",FACE,{"disambiguationData":[OSD([subQ2])]});var subQ4=makeQuery(id+"F15.opExtrude","SWEPT_FACE",FACE,{"disambiguationData":[OSD([sQuery(id+"F14.wireOp",EDGE,"E13.right")])]});var subQ5=makeQuery(id+"F15.boolean.opBoolean","MERGE",FACE,{"derivedFrom":[subQ1,subQ3,subQ4]});var subQ6=makeQuery(id+"F17.opExtrude","SWEPT_FACE",FACE,{"disambiguationData":[OSD([sQuery(id+"F16.wireOp",EDGE,"E15.left")])]});var subQ7=makeQuery(id+"F9.opExtrude","SWEPT_FACE",FACE,{"disambiguationData":[OSD([sQuery(id+"F8.wireOp",EDGE,"E10.right")])]});var subQ8=makeQuery(id+"F17.opExtrude","SWEPT_FACE",FACE,{"disambiguationData":[OSD([sQuery(id+"F16.wireOp",EDGE,"E15.right")])]});var subQ9=makeQuery(id+"F9.opExtrude","SWEPT_FACE",FACE,{"disambiguationData":[OSD([sQuery(id+"F8.wireOp",EDGE,"E10.left")])]});var subQ10=makeQuery(id+"F1.opExtrude","SWEPT_FACE",FACE,{"disambiguationData":[OSD([sQuery(id+"F0.wireOp",EDGE,"E1.bottom")])]});var subQ11=sQuery(id+"F2.wireOp",EDGE,"E2.bottom");var subQ12=sQuery(id+"F2.wireOp",EDGE,"E2.top");var subQ13=sQuery(id+"F4.wireOp",EDGE,"E6.top");var subQ14=makeQuery(id+"F5.opExtrude","SWEPT_FACE",FACE,{"disambiguationData":[OSD([subQ13])]});var subQ15=makeQuery(id+"F17.opExtrude","SWEPT_FACE",FACE,{"disambiguationData":[OSD([sQuery(id+"F16.wireOp",EDGE,"E15.bottom")])]});var subQ16=makeQuery(id+"F3.opExtrude","SWEPT_FACE",FACE,{"disambiguationData":[OSD([subQ11])]});var subQ17=makeQuery(id+"F1.opExtrude","SWEPT_FACE",FACE,{"disambiguationData":[OSD([sQuery(id+"F0.wireOp",EDGE,"E0.bottom")])]});var subQ18=makeQuery(id+"F3.opExtrude","SWEPT_FACE",FACE,{"disambiguationData":[OSD([subQ12])]});var subQ19=makeQuery(id+"F3.opExtrude","SWEPT_FACE",FACE,{"disambiguationData":[OSD([sQuery(id+"F2.wireOp",EDGE,"E5.bottom")])]});var subQ20=makeQuery(id+"F15.opExtrude","SWEPT_FACE",FACE,{"disambiguationData":[OSD([sQuery(id+"F14.wireOp",EDGE,"E13.bottom")])]});var subQ21=makeQuery(id+"F3.opExtrude","SWEPT_FACE",FACE,{"disambiguationData":[OSD([sQuery(id+"F2.wireOp",EDGE,"E5.top")])]});var subQ22=sQuery(id+"F2.wireOp",EDGE,"E3.bottom");var subQ23=sQuery(id+"F2.wireOp",EDGE,"E3.top");var subQ24=sQuery(id+"F4.wireOp",EDGE,"E7.top");var subQ25=makeQuery(id+"F23.opExtrude","SWEPT_FACE",FACE,{"disambiguationData":[OSD([sQuery(id+"F22.wireOp",EDGE,"E18.right")])]});Q0=makeQuery(id+"FUZoe6oa8cMinL2_1.boolean.opBoolean","MERGE",FACE,{"derivedFrom":[makeQuery(id+"F27.opExtrude","SWEPT_FACE",FACE,{"disambiguationData":[OSD([sQuery(id+"F26.wireOp",EDGE,"E22.left")])]}),makeQuery(id+"F27.boolean.opBoolean","MERGE",FACE,{"derivedFrom":[makeQuery(id+"F25.boolean.opBoolean","SPLIT",FACE,{"disambiguationData":[TD([subQ17])],"derivedFrom":makeQuery(id+"F23.boolean.opBoolean","MERGE",FACE,{"derivedFrom":[makeQuery(id+"F17.boolean.opBoolean","SPLIT",FACE,{"disambiguationData":[TD([subQ17,subQ10,subQ16,makeQuery(id+"F3.opExtrude","CAP_FACE",FACE,{"disambiguationData":[OSD([subQ11,subQ12,sQuery(id+"F2.wireOp",EDGE,"E2.left"),subQ0])],"isStart":false}),subQ18,subQ1,subQ3,subQ19,subQ21,subQ14,subQ9,subQ7,subQ20,subQ4,subQ15,subQ6,subQ8])],"derivedFrom":subQ5}),makeQuery(id+"F17.boolean.opBoolean","SPLIT",FACE,{"disambiguationData":[TD([makeQuery(id+"F1.opExtrude","SWEPT_FACE",FACE,{"disambiguationData":[OSD([sQuery(id+"F0.wireOp",EDGE,"E0.top")])]}),makeQuery(id+"F1.opExtrude","SWEPT_FACE",FACE,{"disambiguationData":[OSD([sQuery(id+"F0.wireOp",EDGE,"E1.top")])]}),subQ1,makeQuery(id+"F3.opExtrude","SWEPT_FACE",FACE,{"disambiguationData":[OSD([subQ22])]}),makeQuery(id+"F3.opExtrude","CAP_FACE",FACE,{"disambiguationData":[OSD([subQ22,subQ23,sQuery(id+"F2.wireOp",EDGE,"E3.left"),subQ2])],"isStart":false}),makeQuery(id+"F3.opExtrude","SWEPT_FACE",FACE,{"disambiguationData":[OSD([subQ23])]}),subQ3,makeQuery(id+"F3.opExtrude","SWEPT_FACE",FACE,{"disambiguationData":[OSD([sQuery(id+"F2.wireOp",EDGE,"E4.bottom")])]}),makeQuery(id+"F3.opExtrude","SWEPT_FACE",FACE,{"disambiguationData":[OSD([sQuery(id+"F2.wireOp",EDGE,"E4.top")])]}),makeQuery(id+"F5.opExtrude","SWEPT_FACE",FACE,{"disambiguationData":[OSD([subQ24])]}),makeQuery(id+"F9.opExtrude","SWEPT_FACE",FACE,{"disambiguationData":[OSD([sQuery(id+"F8.wireOp",EDGE,"E9.left")])]}),makeQuery(id+"F9.opExtrude","SWEPT_FACE",FACE,{"disambiguationData":[OSD([sQuery(id+"F8.wireOp",EDGE,"E9.right")])]}),subQ20,subQ4,makeQuery(id+"F17.opExtrude","SWEPT_FACE",FACE,{"disambiguationData":[OSD([sQuery(id+"F16.wireOp",EDGE,"E14.bottom")])]}),makeQuery(id+"F17.opExtrude","SWEPT_FACE",FACE,{"disambiguationData":[OSD([sQuery(id+"F16.wireOp",EDGE,"E14.left")])]}),makeQuery(id+"F17.opExtrude","SWEPT_FACE",FACE,{"disambiguationData":[OSD([sQuery(id+"F16.wireOp",EDGE,"E14.right")])]})])],"derivedFrom":subQ5}),subQ25]})}),makeQuery(id+"F27.opExtrude","SWEPT_FACE",FACE,{"disambiguationData":[OSD([sQuery(id+"F26.wireOp",EDGE,"E24.left")])]})]}),makeQuery(id+"FUZoe6oa8cMinL2_1.opExtrude","SWEPT_FACE",FACE,{"disambiguationData":[OSD([sQuery(id+"FOtPPX5zzCYf9th_1.wireOp",EDGE,"2fd6932c-7f1c-46cd-a8b2-83562e5771d5.left")])]})]});}
            var sketch = newSketch(context, id + "F28", { "sketchPlane" : qUnion([Q0])});
            skLineSegment(sketch, "E25.bottom", {"start": v(580.1, 1360) * mm, "end": v(560.1, 1360) * mm});
            skLineSegment(sketch, "E25.top", {"start": v(580.1, 1340) * mm, "end": v(560.1, 1340) * mm});
            skLineSegment(sketch, "E25.left", {"start": v(580.1, 1360) * mm, "end": v(580.1, 1340) * mm});
            skLineSegment(sketch, "E25.right", {"start": v(560.1, 1360) * mm, "end": v(560.1, 1340) * mm});
            skSolve(sketch);
        }
        {
            var Q0;
            Q0 = qSketchRegion(id + "F28", true);
            extrude(context, id + "F29", {"entities" : qUnion([Q0]), "operationType" : NewBodyOperationType.ADD, "endBound" : BoundingType.UP_TO_NEXT, "depth" : 25 * mm});
        }
        {
            var Q0;
            {var subQ0=sQuery(id+"F0.wireOp",EDGE,"E1.bottom");var subQ1=makeQuery(id+"F1.opExtrude","SWEPT_FACE",FACE,{"disambiguationData":[OSD([subQ0])]});var subQ2=sQuery(id+"F2.wireOp",EDGE,"E5.top");var subQ3=makeQuery(id+"F3.opExtrude","SWEPT_FACE",FACE,{"disambiguationData":[OSD([subQ2])]});var subQ4=makeQuery(id+"F9.opExtrude","SWEPT_FACE",FACE,{"disambiguationData":[OSD([sQuery(id+"F8.wireOp",EDGE,"E10.right")])]});var subQ5=makeQuery(id+"F17.opExtrude","SWEPT_FACE",FACE,{"disambiguationData":[OSD([sQuery(id+"F16.wireOp",EDGE,"E15.left")])]});var subQ6=makeQuery(id+"F25.opExtrude","SWEPT_FACE",FACE,{"disambiguationData":[OSD([sQuery(id+"F24.wireOp",EDGE,"E20.left")])]});var subQ7=makeQuery(id+"FmlsiqtGIArLWjF_1.opExtrude","SWEPT_FACE",FACE,{"disambiguationData":[OSD([sQuery(id+"F9PASD7YzdcTaxW_1.wireOp",EDGE,"aaf027d5-d421-491f-bd49-f5003cbc895b.bottom")])]});var subQ8=makeQuery(id+"FmlsiqtGIArLWjF_1.opExtrude","SWEPT_FACE",FACE,{"disambiguationData":[OSD([sQuery(id+"F9PASD7YzdcTaxW_1.wireOp",EDGE,"8c24dee2-4859-4918-b62b-53ab4d53a5c6.bottom")])]});var subQ9=makeQuery(id+"F85Uv7rZhHDFAwa_1.opExtrude","SWEPT_FACE",FACE,{"disambiguationData":[OSD([sQuery(id+"FFAFteAvz5Cuugt_1.wireOp",EDGE,"0af742db-d6e2-4e39-92e2-1c10abb64e47.left")])]});var subQ19=sQuery(id+"F0.wireOp",EDGE,"E1.left");Q0=makeQuery(id+"Ff9F8cMuZfDcDKN_1.boolean.opBoolean","SPLIT",FACE,{"disambiguationData":[TD([makeQuery(id+"F1.opExtrude","SWEPT_FACE",FACE,{"disambiguationData":[OSD([subQ19])]})])],"derivedFrom":makeQuery(id+"F85Uv7rZhHDFAwa_1.boolean.opBoolean","MERGE",FACE,{"derivedFrom":[makeQuery(id+"FmlsiqtGIArLWjF_1.boolean.opBoolean","MERGE",FACE,{"derivedFrom":[makeQuery(id+"F25.boolean.opBoolean","MERGE",FACE,{"derivedFrom":[makeQuery(id+"F17.boolean.opBoolean","MERGE",FACE,{"derivedFrom":[makeQuery(id+"F9.boolean.opBoolean","MERGE",FACE,{"derivedFrom":[makeQuery(id+"F3.boolean.opBoolean","MERGE",FACE,{"derivedFrom":[subQ1,subQ3]}),subQ4]}),subQ5]}),subQ6]}),subQ7,subQ8]}),subQ9]})});}
            var sketch = newSketch(context, id + "F30", { "sketchPlane" : qUnion([Q0])});
            skLineSegment(sketch, "E26.bottom", {"start": v(379.49, 0) * mm, "end": v(299.49, 0) * mm});
            skLineSegment(sketch, "E26.top", {"start": v(379.49, 3) * mm, "end": v(299.49, 3) * mm});
            skLineSegment(sketch, "E26.left", {"start": v(379.49, 0) * mm, "end": v(379.49, 3) * mm});
            skLineSegment(sketch, "E26.right", {"start": v(299.49, 0) * mm, "end": v(299.49, 3) * mm});
            skLineSegment(sketch, "E27.bottom", {"start": v(-80.51, 0) * mm, "end": v(-0.51, 0) * mm});
            skLineSegment(sketch, "E27.top", {"start": v(-80.51, 3) * mm, "end": v(-0.51, 3) * mm});
            skLineSegment(sketch, "E27.left", {"start": v(-80.51, 0) * mm, "end": v(-80.51, 3) * mm});
            skLineSegment(sketch, "E27.right", {"start": v(-0.51, 0) * mm, "end": v(-0.51, 3) * mm});
            skSolve(sketch);
        }
        {
            var Q0;
            Q0 = qSketchRegion(id + "F30", true);
            extrude(context, id + "F31", {"entities" : qUnion([Q0]), "operationType" : NewBodyOperationType.ADD, "endBound" : BoundingType.UP_TO_NEXT, "depth" : 25 * mm});
        }
        {
            var Q0;
            Q0=makeQuery(id+"F13.opExtrude","SWEPT_FACE",FACE,{"disambiguationData":[OSD([sQuery(id+"F12.wireOp",EDGE,"E12.right")])]});
            var sketch = newSketch(context, id + "F32", { "sketchPlane" : qUnion([Q0])});
            skLineSegment(sketch, "E28.bottom", {"start": v(379.49, 3) * mm, "end": v(299.49, 3) * mm});
            skLineSegment(sketch, "E28.top", {"start": v(379.49, 0) * mm, "end": v(299.49, 0) * mm});
            skLineSegment(sketch, "E28.left", {"start": v(379.49, 3) * mm, "end": v(379.49, 0) * mm});
            skLineSegment(sketch, "E28.right", {"start": v(299.49, 3) * mm, "end": v(299.49, 0) * mm});
            skLineSegment(sketch, "E29.bottom", {"start": v(-80.51, 3) * mm, "end": v(-0.51, 3) * mm});
            skLineSegment(sketch, "E29.top", {"start": v(-80.51, 0) * mm, "end": v(-0.51, 0) * mm});
            skLineSegment(sketch, "E29.left", {"start": v(-80.51, 3) * mm, "end": v(-80.51, 0) * mm});
            skLineSegment(sketch, "E29.right", {"start": v(-0.51, 3) * mm, "end": v(-0.51, 0) * mm});
            skSolve(sketch);
        }
        {
            var Q0;
            Q0 = qSketchRegion(id + "F32", true);
            extrude(context, id + "F33", {"entities" : qUnion([Q0]), "operationType" : NewBodyOperationType.ADD, "endBound" : BoundingType.UP_TO_NEXT, "depth" : 25 * mm});
        }
        {
            var Q0;
            {var subQ0=sQuery(id+"F2.wireOp",EDGE,"E2.right");var subQ1=makeQuery(id+"F3.opExtrude","SWEPT_FACE",FACE,{"disambiguationData":[OSD([subQ0])]});var subQ2=sQuery(id+"F2.wireOp",EDGE,"E3.right");var subQ3=makeQuery(id+"F3.opExtrude","SWEPT_FACE",FACE,{"disambiguationData":[OSD([subQ2])]});var subQ4=makeQuery(id+"F15.opExtrude","SWEPT_FACE",FACE,{"disambiguationData":[OSD([sQuery(id+"F14.wireOp",EDGE,"E13.right")])]});var subQ5=makeQuery(id+"F15.boolean.opBoolean","MERGE",FACE,{"derivedFrom":[subQ1,subQ3,subQ4]});var subQ6=makeQuery(id+"F17.opExtrude","SWEPT_FACE",FACE,{"disambiguationData":[OSD([sQuery(id+"F16.wireOp",EDGE,"E15.left")])]});var subQ7=makeQuery(id+"F9.opExtrude","SWEPT_FACE",FACE,{"disambiguationData":[OSD([sQuery(id+"F8.wireOp",EDGE,"E10.right")])]});var subQ8=makeQuery(id+"F17.opExtrude","SWEPT_FACE",FACE,{"disambiguationData":[OSD([sQuery(id+"F16.wireOp",EDGE,"E15.right")])]});var subQ9=makeQuery(id+"F9.opExtrude","SWEPT_FACE",FACE,{"disambiguationData":[OSD([sQuery(id+"F8.wireOp",EDGE,"E10.left")])]});var subQ10=makeQuery(id+"F1.opExtrude","SWEPT_FACE",FACE,{"disambiguationData":[OSD([sQuery(id+"F0.wireOp",EDGE,"E1.bottom")])]});var subQ11=sQuery(id+"F2.wireOp",EDGE,"E2.bottom");var subQ12=sQuery(id+"F2.wireOp",EDGE,"E2.top");var subQ13=sQuery(id+"F4.wireOp",EDGE,"E6.top");var subQ14=makeQuery(id+"F5.opExtrude","SWEPT_FACE",FACE,{"disambiguationData":[OSD([subQ13])]});var subQ15=makeQuery(id+"F17.opExtrude","SWEPT_FACE",FACE,{"disambiguationData":[OSD([sQuery(id+"F16.wireOp",EDGE,"E15.bottom")])]});var subQ16=makeQuery(id+"F3.opExtrude","SWEPT_FACE",FACE,{"disambiguationData":[OSD([subQ11])]});var subQ17=makeQuery(id+"F1.opExtrude","SWEPT_FACE",FACE,{"disambiguationData":[OSD([sQuery(id+"F0.wireOp",EDGE,"E0.bottom")])]});var subQ18=makeQuery(id+"F3.opExtrude","SWEPT_FACE",FACE,{"disambiguationData":[OSD([subQ12])]});var subQ19=makeQuery(id+"F3.opExtrude","SWEPT_FACE",FACE,{"disambiguationData":[OSD([sQuery(id+"F2.wireOp",EDGE,"E5.bottom")])]});var subQ20=makeQuery(id+"F15.opExtrude","SWEPT_FACE",FACE,{"disambiguationData":[OSD([sQuery(id+"F14.wireOp",EDGE,"E13.bottom")])]});var subQ21=makeQuery(id+"F3.opExtrude","SWEPT_FACE",FACE,{"disambiguationData":[OSD([sQuery(id+"F2.wireOp",EDGE,"E5.top")])]});var subQ22=sQuery(id+"F2.wireOp",EDGE,"E3.bottom");var subQ23=sQuery(id+"F2.wireOp",EDGE,"E3.top");var subQ24=sQuery(id+"F4.wireOp",EDGE,"E7.top");var subQ25=makeQuery(id+"F23.opExtrude","SWEPT_FACE",FACE,{"disambiguationData":[OSD([sQuery(id+"F22.wireOp",EDGE,"E18.right")])]});Q0=makeQuery(id+"F27.boolean.opBoolean","MERGE",FACE,{"derivedFrom":[makeQuery(id+"F25.boolean.opBoolean","SPLIT",FACE,{"disambiguationData":[TD([subQ17])],"derivedFrom":makeQuery(id+"F23.boolean.opBoolean","MERGE",FACE,{"derivedFrom":[makeQuery(id+"F17.boolean.opBoolean","SPLIT",FACE,{"disambiguationData":[TD([subQ17,subQ10,subQ16,makeQuery(id+"F3.opExtrude","CAP_FACE",FACE,{"disambiguationData":[OSD([subQ11,subQ12,sQuery(id+"F2.wireOp",EDGE,"E2.left"),subQ0])],"isStart":false}),subQ18,subQ1,subQ3,subQ19,subQ21,subQ14,subQ9,subQ7,subQ20,subQ4,subQ15,subQ6,subQ8])],"derivedFrom":subQ5}),makeQuery(id+"F17.boolean.opBoolean","SPLIT",FACE,{"disambiguationData":[TD([makeQuery(id+"F1.opExtrude","SWEPT_FACE",FACE,{"disambiguationData":[OSD([sQuery(id+"F0.wireOp",EDGE,"E0.top")])]}),makeQuery(id+"F1.opExtrude","SWEPT_FACE",FACE,{"disambiguationData":[OSD([sQuery(id+"F0.wireOp",EDGE,"E1.top")])]}),subQ1,makeQuery(id+"F3.opExtrude","SWEPT_FACE",FACE,{"disambiguationData":[OSD([subQ22])]}),makeQuery(id+"F3.opExtrude","CAP_FACE",FACE,{"disambiguationData":[OSD([subQ22,subQ23,sQuery(id+"F2.wireOp",EDGE,"E3.left"),subQ2])],"isStart":false}),makeQuery(id+"F3.opExtrude","SWEPT_FACE",FACE,{"disambiguationData":[OSD([subQ23])]}),subQ3,makeQuery(id+"F3.opExtrude","SWEPT_FACE",FACE,{"disambiguationData":[OSD([sQuery(id+"F2.wireOp",EDGE,"E4.bottom")])]}),makeQuery(id+"F3.opExtrude","SWEPT_FACE",FACE,{"disambiguationData":[OSD([sQuery(id+"F2.wireOp",EDGE,"E4.top")])]}),makeQuery(id+"F5.opExtrude","SWEPT_FACE",FACE,{"disambiguationData":[OSD([subQ24])]}),makeQuery(id+"F9.opExtrude","SWEPT_FACE",FACE,{"disambiguationData":[OSD([sQuery(id+"F8.wireOp",EDGE,"E9.left")])]}),makeQuery(id+"F9.opExtrude","SWEPT_FACE",FACE,{"disambiguationData":[OSD([sQuery(id+"F8.wireOp",EDGE,"E9.right")])]}),subQ20,subQ4,makeQuery(id+"F17.opExtrude","SWEPT_FACE",FACE,{"disambiguationData":[OSD([sQuery(id+"F16.wireOp",EDGE,"E14.bottom")])]}),makeQuery(id+"F17.opExtrude","SWEPT_FACE",FACE,{"disambiguationData":[OSD([sQuery(id+"F16.wireOp",EDGE,"E14.left")])]}),makeQuery(id+"F17.opExtrude","SWEPT_FACE",FACE,{"disambiguationData":[OSD([sQuery(id+"F16.wireOp",EDGE,"E14.right")])]})])],"derivedFrom":subQ5}),subQ25]})}),makeQuery(id+"F27.opExtrude","SWEPT_FACE",FACE,{"disambiguationData":[OSD([sQuery(id+"F26.wireOp",EDGE,"E24.left")])]})]});}
            var sketch = newSketch(context, id + "F34", { "sketchPlane" : qUnion([Q0])});
            skLineSegment(sketch, "E30.bottom", {"start": v(560.1, 1310) * mm, "end": v(580.1, 1310) * mm});
            skLineSegment(sketch, "E30.top", {"start": v(560.1, 1290) * mm, "end": v(580.1, 1290) * mm});
            skLineSegment(sketch, "E30.left", {"start": v(560.1, 1310) * mm, "end": v(560.1, 1290) * mm});
            skLineSegment(sketch, "E30.right", {"start": v(580.1, 1310) * mm, "end": v(580.1, 1290) * mm});
            skSolve(sketch);
        }
        {
            var Q0;
            Q0 = qSketchRegion(id + "F34", true);
            extrude(context, id + "F35", {"entities" : qUnion([Q0]), "operationType" : NewBodyOperationType.ADD, "endBound" : BoundingType.UP_TO_NEXT, "depth" : 25 * mm});
        }
        {
            var Q0;
            Q0=makeQuery(id+"F21.boolean.opBoolean","MERGE",FACE,{"derivedFrom":[makeQuery(id+"F9.boolean.opBoolean","MERGE",FACE,{"derivedFrom":[makeQuery(id+"F7.boolean.opBoolean","MERGE",FACE,{"derivedFrom":[makeQuery(id+"F5.opExtrude","CAP_FACE",FACE,{"disambiguationData":[OSD([sQuery(id+"F4.wireOp",EDGE,"E6.bottom"),sQuery(id+"F4.wireOp",EDGE,"E6.top"),sQuery(id+"F4.wireOp",EDGE,"E6.left"),sQuery(id+"F4.wireOp",EDGE,"E6.right")])],"isStart":false}),makeQuery(id+"F5.opExtrude","CAP_FACE",FACE,{"disambiguationData":[OSD([sQuery(id+"F4.wireOp",EDGE,"E7.bottom"),sQuery(id+"F4.wireOp",EDGE,"E7.top"),sQuery(id+"F4.wireOp",EDGE,"E7.left"),sQuery(id+"F4.wireOp",EDGE,"E7.right")])],"isStart":false}),makeQuery(id+"F7.opExtrude","SWEPT_FACE",FACE,{"disambiguationData":[OSD([sQuery(id+"F6.wireOp",EDGE,"E8.bottom")])]})]}),makeQuery(id+"F9.opExtrude","SWEPT_FACE",FACE,{"disambiguationData":[OSD([sQuery(id+"F8.wireOp",EDGE,"E9.top")])]}),makeQuery(id+"F9.opExtrude","SWEPT_FACE",FACE,{"disambiguationData":[OSD([sQuery(id+"F8.wireOp",EDGE,"E10.bottom")])]})]}),makeQuery(id+"F15.opExtrude","SWEPT_FACE",FACE,{"disambiguationData":[OSD([sQuery(id+"F14.wireOp",EDGE,"E13.bottom")])]}),makeQuery(id+"F21.opExtrude","SWEPT_FACE",FACE,{"disambiguationData":[OSD([sQuery(id+"F20.wireOp",EDGE,"E17.top")])]})]});
            cPlane(context, id + "F36", {"entities" : qUnion([Q0]), "cplaneType" : CPlaneType.OFFSET, "offset" : 1 * mm, "width" : 150 * mm, "height" : 150 * mm});
        }
        {
            var Q0;
            Q0=qCreatedBy(id+"F36.planeOp",FACE);
            var sketch = newSketch(context, id + "F37", { "sketchPlane" : qUnion([Q0])});
            skLineSegment(sketch, "E31.bottom", {"start": v(-98.27, -457.36) * mm, "end": v(421.73, -457.36) * mm});
            skLineSegment(sketch, "E31.top", {"start": v(-98.27, 492.64) * mm, "end": v(421.73, 492.64) * mm});
            skLineSegment(sketch, "E31.left", {"start": v(-98.27, -457.36) * mm, "end": v(-98.27, 492.64) * mm});
            skLineSegment(sketch, "E31.right", {"start": v(421.73, -457.36) * mm, "end": v(421.73, 492.64) * mm});
            skSolve(sketch);
        }
        {
            var Q0;
            Q0 = qSketchRegion(id + "F37", true);
            extrude(context, id + "F38", {"entities" : qUnion([Q0]), "operationType" : NewBodyOperationType.ADD, "depth" : 12 * mm});
        }
        {
            var Q0;
            Q0=makeQuery(id+"F38.opExtrude","CAP_FACE",FACE,{"disambiguationData":[OSD([sQuery(id+"F37.wireOp",EDGE,"E31.bottom"),sQuery(id+"F37.wireOp",EDGE,"E31.top"),sQuery(id+"F37.wireOp",EDGE,"E31.left"),sQuery(id+"F37.wireOp",EDGE,"E31.right")])],"isStart":false});
            var sketch = newSketch(context, id + "F39", { "sketchPlane" : qUnion([Q0])});
            skLineSegment(sketch, "E32.bottom", {"start": v(-62.4, -407.36) * mm, "end": v(382.6, -407.36) * mm});
            skLineSegment(sketch, "E32.top", {"start": v(-62.4, -27.36) * mm, "end": v(382.6, -27.36) * mm});
            skLineSegment(sketch, "E32.left", {"start": v(-62.4, -407.36) * mm, "end": v(-62.4, -27.36) * mm});
            skLineSegment(sketch, "E32.right", {"start": v(382.6, -407.36) * mm, "end": v(382.6, -27.36) * mm});
            skSolve(sketch);
        }
        {
            var Q0;
            Q0 = qSketchRegion(id + "F39", true);
            extrude(context, id + "F40", {"entities" : qUnion([Q0]), "operationType" : NewBodyOperationType.REMOVE, "oppositeDirection" : true, "depth" : 25 * mm});
        }
        {
            var Q0;
            Q0=makeQuery(id+"F38.opExtrude","SWEPT_FACE",FACE,{"disambiguationData":[OSD([sQuery(id+"F37.wireOp",EDGE,"E31.bottom")])]});
            var sketch = newSketch(context, id + "F41", { "sketchPlane" : qUnion([Q0])});
            skLineSegment(sketch, "E33.bottom", {"start": v(-74.81, 933) * mm, "end": v(171, 933) * mm});
            skLineSegment(sketch, "E33.top", {"start": v(-74.81, 921) * mm, "end": v(171, 921) * mm});
            skLineSegment(sketch, "E33.left", {"start": v(-74.81, 933) * mm, "end": v(-74.81, 921) * mm});
            skLineSegment(sketch, "E33.right", {"start": v(171, 933) * mm, "end": v(171, 921) * mm});
            skLineSegment(sketch, "E34.bottom", {"start": v(203.83, 933) * mm, "end": v(421.73, 933) * mm});
            skLineSegment(sketch, "E34.top", {"start": v(203.83, 921) * mm, "end": v(421.73, 921) * mm});
            skLineSegment(sketch, "E34.left", {"start": v(203.83, 933) * mm, "end": v(203.83, 921) * mm});
            skLineSegment(sketch, "E34.right", {"start": v(421.73, 933) * mm, "end": v(421.73, 921) * mm});
            skSolve(sketch);
        }
        {
            var Q0;
            Q0 = qSketchRegion(id + "F41", true);
            extrude(context, id + "F42", {"entities" : qUnion([Q0]), "operationType" : NewBodyOperationType.ADD, "depth" : 25 * mm});
        }
        {
            var Q0;
            Q0=makeQuery(id+"F38.opExtrude","SWEPT_FACE",FACE,{"disambiguationData":[OSD([sQuery(id+"F37.wireOp",EDGE,"E31.top")])]});
            var sketch = newSketch(context, id + "F43", { "sketchPlane" : qUnion([Q0])});
            skLineSegment(sketch, "E35.bottom", {"start": v(-421.73, 933) * mm, "end": v(-210.83, 933) * mm});
            skLineSegment(sketch, "E35.top", {"start": v(-421.73, 921) * mm, "end": v(-210.83, 921) * mm});
            skLineSegment(sketch, "E35.left", {"start": v(-421.73, 933) * mm, "end": v(-421.73, 921) * mm});
            skLineSegment(sketch, "E35.right", {"start": v(-210.83, 933) * mm, "end": v(-210.83, 921) * mm});
            skLineSegment(sketch, "E36.bottom", {"start": v(-174.03, 933) * mm, "end": v(73.9, 933) * mm});
            skLineSegment(sketch, "E36.top", {"start": v(-174.03, 921) * mm, "end": v(73.9, 921) * mm});
            skLineSegment(sketch, "E36.left", {"start": v(-174.03, 933) * mm, "end": v(-174.03, 921) * mm});
            skLineSegment(sketch, "E36.right", {"start": v(73.9, 933) * mm, "end": v(73.9, 921) * mm});
            skSolve(sketch);
        }
        {
            var Q0;
            Q0 = qSketchRegion(id + "F43", true);
            extrude(context, id + "F44", {"entities" : qUnion([Q0]), "operationType" : NewBodyOperationType.ADD, "depth" : 30 * mm});
        }
        {
            var Q0;
            Q0=makeQuery(id+"F44.boolean.opBoolean","MERGE",FACE,{"derivedFrom":[makeQuery(id+"F42.boolean.opBoolean","MERGE",FACE,{"derivedFrom":[makeQuery(id+"FcAkgqnoUZr5R8B_2.boolean.opBoolean","MERGE",FACE,{"derivedFrom":[makeQuery(id+"F38.opExtrude","CAP_FACE",FACE,{"disambiguationData":[OSD([sQuery(id+"F37.wireOp",EDGE,"E31.bottom"),sQuery(id+"F37.wireOp",EDGE,"E31.top"),sQuery(id+"F37.wireOp",EDGE,"E31.left"),sQuery(id+"F37.wireOp",EDGE,"E31.right")])],"isStart":false}),makeQuery(id+"FcAkgqnoUZr5R8B_2.opExtrude","SWEPT_FACE",FACE,{"disambiguationData":[OSD([sQuery(id+"FsmpxHjDU3ubDs0_2.wireOp",EDGE,"o6ZRnpyB-D6iB-rqNJ-Y9P0-ViHlPvLhDTKM.bottom")])]})]}),makeQuery(id+"F42.opExtrude","SWEPT_FACE",FACE,{"disambiguationData":[OSD([sQuery(id+"F41.wireOp",EDGE,"E33.bottom")])]})]}),makeQuery(id+"F44.opExtrude","SWEPT_FACE",FACE,{"disambiguationData":[OSD([sQuery(id+"F43.wireOp",EDGE,"E35.bottom")])]}),makeQuery(id+"F44.opExtrude","SWEPT_FACE",FACE,{"disambiguationData":[OSD([sQuery(id+"F43.wireOp",EDGE,"E36.bottom")])]})]});
            cPlane(context, id + "F45", {"entities" : qUnion([Q0]), "cplaneType" : CPlaneType.OFFSET, "offset" : 1 * mm, "width" : 150 * mm, "height" : 150 * mm});
        }
        {
            var Q0;
            Q0=qCreatedBy(id+"F45.planeOp",FACE);
            var sketch = newSketch(context, id + "F46", { "sketchPlane" : qUnion([Q0])});
            skLineSegment(sketch, "E37.bottom", {"start": v(-79.66, -458.2) * mm, "end": v(-67.66, -458.2) * mm});
            skLineSegment(sketch, "E37.top", {"start": v(-79.66, 491.8) * mm, "end": v(-67.66, 491.8) * mm});
            skLineSegment(sketch, "E37.left", {"start": v(-79.66, -458.2) * mm, "end": v(-79.66, 491.8) * mm});
            skLineSegment(sketch, "E37.right", {"start": v(-67.66, -458.2) * mm, "end": v(-67.66, 491.8) * mm});
            skSolve(sketch);
        }
        {
            var Q0;
            Q0 = qSketchRegion(id + "F46", true);
            extrude(context, id + "F47", {"entities" : qUnion([Q0]), "depth" : 550 * mm});
        }
        {
            var Q0;
            Q0=makeQuery(id+"F47.opExtrude","SWEPT_FACE",FACE,{"disambiguationData":[OSD([sQuery(id+"F46.wireOp",EDGE,"E37.bottom")])]});
            var sketch = newSketch(context, id + "F48", { "sketchPlane" : qUnion([Q0])});
            skLineSegment(sketch, "E38.bottom", {"start": v(-67.66, 934) * mm, "end": v(-79.66, 934) * mm});
            skLineSegment(sketch, "E38.top", {"start": v(-67.66, 1333.12) * mm, "end": v(-79.66, 1333.12) * mm});
            skLineSegment(sketch, "E38.left", {"start": v(-67.66, 934) * mm, "end": v(-67.66, 1333.12) * mm});
            skLineSegment(sketch, "E38.right", {"start": v(-79.66, 934) * mm, "end": v(-79.66, 1333.12) * mm});
            skSolve(sketch);
        }
        {
            var Q0;
            Q0 = qSketchRegion(id + "F48", true);
            extrude(context, id + "F49", {"entities" : qUnion([Q0]), "operationType" : NewBodyOperationType.ADD, "depth" : 25 * mm});
        }
        {
            var Q0;
            Q0=qCreatedBy(id+"F45.planeOp",FACE);
            var sketch = newSketch(context, id + "F50", { "sketchPlane" : qUnion([Q0])});
            skLineSegment(sketch, "E39.bottom", {"start": v(-66.09, 497.4) * mm, "end": v(333.91, 497.4) * mm});
            skLineSegment(sketch, "E39.top", {"start": v(-66.09, 485.4) * mm, "end": v(333.91, 485.4) * mm});
            skLineSegment(sketch, "E39.left", {"start": v(-66.09, 497.4) * mm, "end": v(-66.09, 485.4) * mm});
            skLineSegment(sketch, "E39.right", {"start": v(333.91, 497.4) * mm, "end": v(333.91, 485.4) * mm});
            skSolve(sketch);
        }
        {
            var Q0;
            Q0 = qSketchRegion(id + "F50", true);
            extrude(context, id + "F51", {"entities" : qUnion([Q0]), "depth" : 425 * mm});
        }
        {
            var Q0;
            Q0=makeQuery(id+"F47.opExtrude","SWEPT_FACE",FACE,{"disambiguationData":[OSD([sQuery(id+"F46.wireOp",EDGE,"E37.top")])]});
            var sketch = newSketch(context, id + "F52", { "sketchPlane" : qUnion([Q0])});
            skLineSegment(sketch, "E40.bottom", {"start": v(79.66, 934) * mm, "end": v(67.66, 934) * mm});
            skLineSegment(sketch, "E40.top", {"start": v(79.66, 1334.16) * mm, "end": v(67.66, 1334.16) * mm});
            skLineSegment(sketch, "E40.left", {"start": v(79.66, 934) * mm, "end": v(79.66, 1334.16) * mm});
            skLineSegment(sketch, "E40.right", {"start": v(67.66, 934) * mm, "end": v(67.66, 1334.16) * mm});
            skSolve(sketch);
        }
        {
            var Q0;
            Q0 = qSketchRegion(id + "F52", true);
            extrude(context, id + "F53", {"entities" : qUnion([Q0]), "operationType" : NewBodyOperationType.ADD, "depth" : 25 * mm});
        }
        {
            var Q0;
            Q0=qCreatedBy(id+"F45.planeOp",FACE);
            var sketch = newSketch(context, id + "F54", { "sketchPlane" : qUnion([Q0])});
            skLineSegment(sketch, "E41.bottom", {"start": v(-66.9, -459.55) * mm, "end": v(233.1, -459.55) * mm});
            skLineSegment(sketch, "E41.top", {"start": v(-66.9, -447.55) * mm, "end": v(233.1, -447.55) * mm});
            skLineSegment(sketch, "E41.left", {"start": v(-66.9, -459.55) * mm, "end": v(-66.9, -447.55) * mm});
            skLineSegment(sketch, "E41.right", {"start": v(233.1, -459.55) * mm, "end": v(233.1, -447.55) * mm});
            skSolve(sketch);
        }
        {
            var Q0;
            Q0 = qSketchRegion(id + "F54", true);
            extrude(context, id + "F55", {"entities" : qUnion([Q0]), "depth" : 425 * mm});
        }
    });
